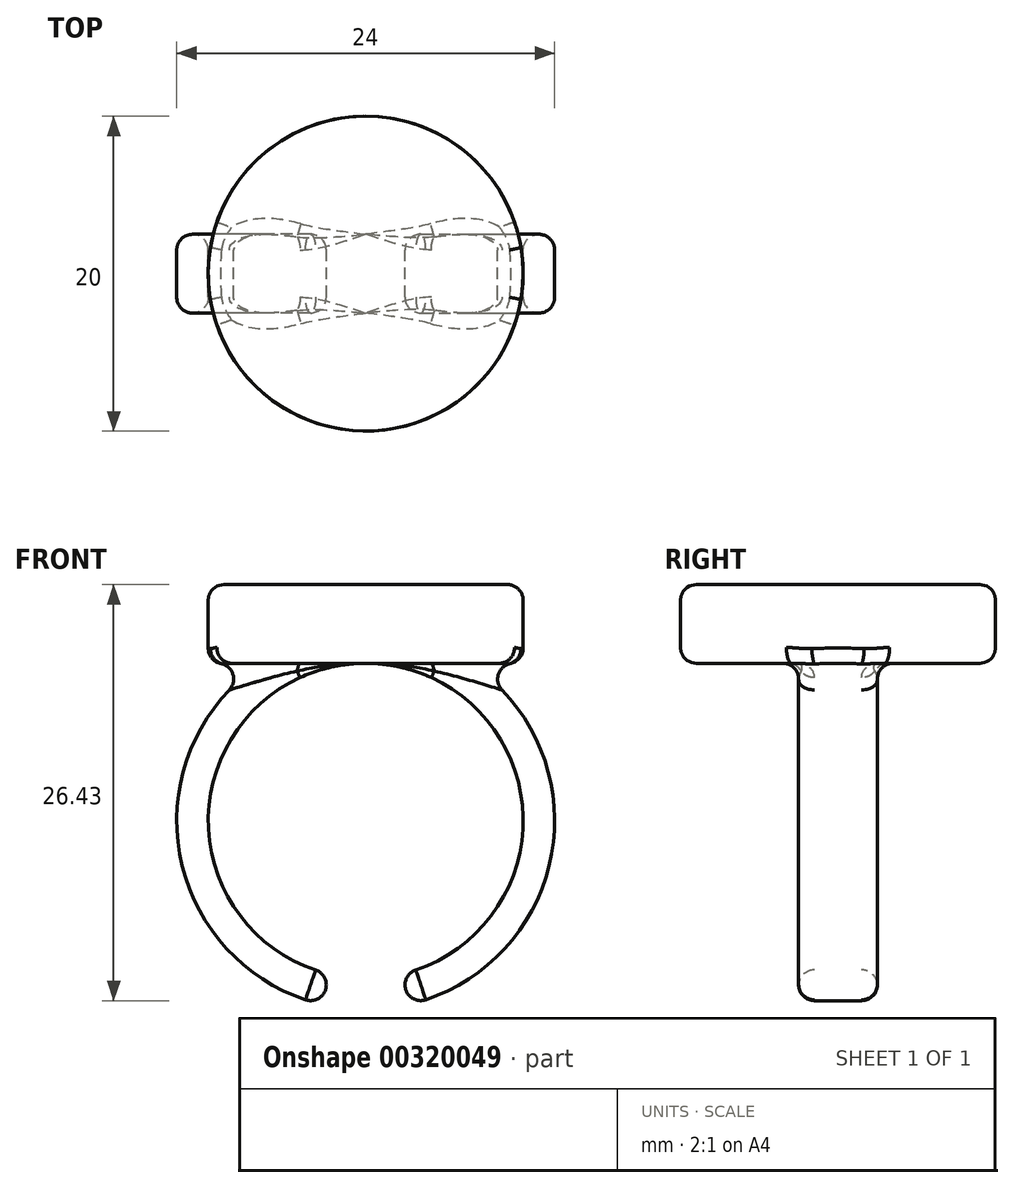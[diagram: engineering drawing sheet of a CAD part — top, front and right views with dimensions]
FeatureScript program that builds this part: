
annotation { "Feature Type Name" : "Feature", "Feature Type Description" : "" }
export const myFeature = defineFeature(function(context is Context, id is Id, definition is map)
    precondition{}
    {
        {
            var Q0;
            Q0=qCreatedBy(makeId("Top.planeOp"),FACE);
            var sketch = newSketch(context, id + "F0", { "sketchPlane" : qUnion([Q0])});
            skCircle(sketch, "E0", {"center": v(0, 0) * mm, "radius": 10 * mm});
            skSolve(sketch);
        }
        {
            var Q0;
            Q0 = qSketchRegion(id + "F0", true);
            extrude(context, id + "F1", {"entities" : qUnion([Q0]), "depth" : 5 * mm});
        }
        {
            var Q0;
            Q0=qCreatedBy(makeId("Front.planeOp"),FACE);
            var sketch = newSketch(context, id + "F2", { "sketchPlane" : qUnion([Q0])});
            skLineSegment(sketch, "E1", {"start": v(0, 0) * mm, "end": v(0, -10) * mm});
            skArc(sketch, "E2", {"start": v(2.5, -19.68) * mm, "mid": v(0, 0) * mm, "end": v(-2.5, -19.68) * mm});
            skArc(sketch, "E3.0", {"start": v(2.5, -21.74) * mm, "mid": v(0, 2) * mm, "end": v(-2.5, -21.74) * mm});
            skLineSegment(sketch, "E4.0", {"start": v(-2.5, -19.68) * mm, "end": v(-2.5, -21.74) * mm});
            skLineSegment(sketch, "E5.0", {"start": v(2.5, -19.68) * mm, "end": v(2.5, -21.74) * mm});
            skPoint(sketch, "E6.orphan", {"position": v(0, -18.4) * mm});
            skSolve(sketch);
        }
        {
            var Q0;
            Q0 = qSketchRegion(id + "F2", true);
            extrude(context, id + "F3", {"entities" : qUnion([Q0]), "operationType" : NewBodyOperationType.ADD, "depth" : 2.5 * mm, "hasSecondDirection" : true, "secondDirectionOppositeDirection" : true, "secondDirectionDepth" : 2.5 * mm});
        }
        {
            var Q0;
            {var subQ0=sQuery(id+"F2.wireOp",EDGE,"E2");var subQ1=sQuery(id+"F2.wireOp",EDGE,"E4.0");Q0=makeQuery(id+"F3.boolean.opBoolean","SPLIT",EDGE,{"disambiguationData":[TD([makeQuery(id+"F3.opExtrude","SWEPT_FACE",FACE,{"disambiguationData":[OSD([subQ1])]})])],"derivedFrom":makeQuery(id+"F3.opExtrude","CAP_EDGE",EDGE,{"disambiguationData":[OSD([subQ0])],"isStart":false})});}
            var Q1;
            {var subQ0=sQuery(id+"F2.wireOp",EDGE,"E2");var subQ1=sQuery(id+"F2.wireOp",EDGE,"E4.0");Q1=makeQuery(id+"F3.boolean.opBoolean","SPLIT",EDGE,{"disambiguationData":[TD([makeQuery(id+"F3.opExtrude","SWEPT_FACE",FACE,{"disambiguationData":[OSD([subQ1])]})])],"derivedFrom":makeQuery(id+"F3.opExtrude","CAP_EDGE",EDGE,{"disambiguationData":[OSD([subQ0])],"isStart":true})});}
            var Q2;
            {var subQ0=sQuery(id+"F2.wireOp",EDGE,"E3.0");var subQ1=sQuery(id+"F2.wireOp",EDGE,"E5.0");Q2=makeQuery(id+"F3.boolean.opBoolean","SPLIT",EDGE,{"disambiguationData":[TD([makeQuery(id+"F3.opExtrude","SWEPT_FACE",FACE,{"disambiguationData":[OSD([subQ1])]})])],"derivedFrom":makeQuery(id+"F3.opExtrude","CAP_EDGE",EDGE,{"disambiguationData":[OSD([subQ0])],"isStart":true})});}
            var Q3;
            {var subQ0=sQuery(id+"F2.wireOp",EDGE,"E3.0");var subQ1=sQuery(id+"F2.wireOp",EDGE,"E5.0");Q3=makeQuery(id+"F3.boolean.opBoolean","SPLIT",EDGE,{"disambiguationData":[TD([makeQuery(id+"F3.opExtrude","SWEPT_FACE",FACE,{"disambiguationData":[OSD([subQ1])]})])],"derivedFrom":makeQuery(id+"F3.opExtrude","CAP_EDGE",EDGE,{"disambiguationData":[OSD([subQ0])],"isStart":false})});}
            var Q4;
            {var subQ0=sQuery(id+"F2.wireOp",EDGE,"E3.0");var subQ1=sQuery(id+"F2.wireOp",EDGE,"E4.0");Q4=makeQuery(id+"F3.boolean.opBoolean","SPLIT",EDGE,{"disambiguationData":[TD([makeQuery(id+"F3.opExtrude","SWEPT_FACE",FACE,{"disambiguationData":[OSD([subQ1])]})])],"derivedFrom":makeQuery(id+"F3.opExtrude","CAP_EDGE",EDGE,{"disambiguationData":[OSD([subQ0])],"isStart":false})});}
            var Q5;
            {var subQ0=sQuery(id+"F2.wireOp",EDGE,"E3.0");var subQ1=sQuery(id+"F2.wireOp",EDGE,"E4.0");Q5=makeQuery(id+"F3.boolean.opBoolean","SPLIT",EDGE,{"disambiguationData":[TD([makeQuery(id+"F3.opExtrude","SWEPT_FACE",FACE,{"disambiguationData":[OSD([subQ1])]})])],"derivedFrom":makeQuery(id+"F3.opExtrude","CAP_EDGE",EDGE,{"disambiguationData":[OSD([subQ0])],"isStart":true})});}
            fillet(context, id + "F4", {"entities" : qUnion([Q0, Q1, Q2, Q3, Q4, Q5]), "radius" : 1 * mm, "tangentPropagation" : true, "allowEdgeOverflow" : false});
        }
        {
            var Q0;
            Q0=makeQuery(id+"F3.opExtrude","SWEPT_FACE",FACE,{"disambiguationData":[OSD([sQuery(id+"F2.wireOp",EDGE,"E4.0")])]});
            var Q1;
            Q1=makeQuery(id+"F3.opExtrude","SWEPT_FACE",FACE,{"disambiguationData":[OSD([sQuery(id+"F2.wireOp",EDGE,"E5.0")])]});
            fillet(context, id + "F5", {"entities" : qUnion([Q0, Q1]), "radius" : 1 * mm, "tangentPropagation" : true, "allowEdgeOverflow" : false});
        }
        {
            var Q0;
            Q0=makeQuery(id+"F3.boolean.opBoolean","INTERSECT",EDGE,{"disambiguationData":[OD(1.0)],"derivedFrom":[makeQuery(id+"F1.opExtrude","CAP_FACE",FACE,{"disambiguationData":[OSD([sQuery(id+"F0.wireOp",EDGE,"E0")])],"isStart":true}),makeQuery(id+"F3.opExtrude","SWEPT_FACE",FACE,{"disambiguationData":[OSD([sQuery(id+"F2.wireOp",EDGE,"E3.0")])]})]});
            var Q1;
            Q1=makeQuery(id+"F3.boolean.opBoolean","INTERSECT",EDGE,{"disambiguationData":[OD(0.0)],"derivedFrom":[makeQuery(id+"F1.opExtrude","CAP_FACE",FACE,{"disambiguationData":[OSD([sQuery(id+"F0.wireOp",EDGE,"E0")])],"isStart":true}),makeQuery(id+"F3.opExtrude","SWEPT_FACE",FACE,{"disambiguationData":[OSD([sQuery(id+"F2.wireOp",EDGE,"E3.0")])]})]});
            fillet(context, id + "F6", {"entities" : qUnion([Q0, Q1]), "radius" : 1 * mm, "tangentPropagation" : true, "allowEdgeOverflow" : false});
        }
        {
            var Q0;
            Q0=makeQuery(id+"F1.opExtrude","CAP_EDGE",EDGE,{"disambiguationData":[OSD([sQuery(id+"F0.wireOp",EDGE,"E0")])],"isStart":false});
            var Q1;
            Q1=makeQuery(id+"F1.opExtrude","CAP_EDGE",EDGE,{"disambiguationData":[OSD([sQuery(id+"F0.wireOp",EDGE,"E0")])],"isStart":true});
            fillet(context, id + "F7", {"entities" : qUnion([Q0, Q1]), "radius" : 1 * mm, "tangentPropagation" : true, "allowEdgeOverflow" : false});
        }
    });
